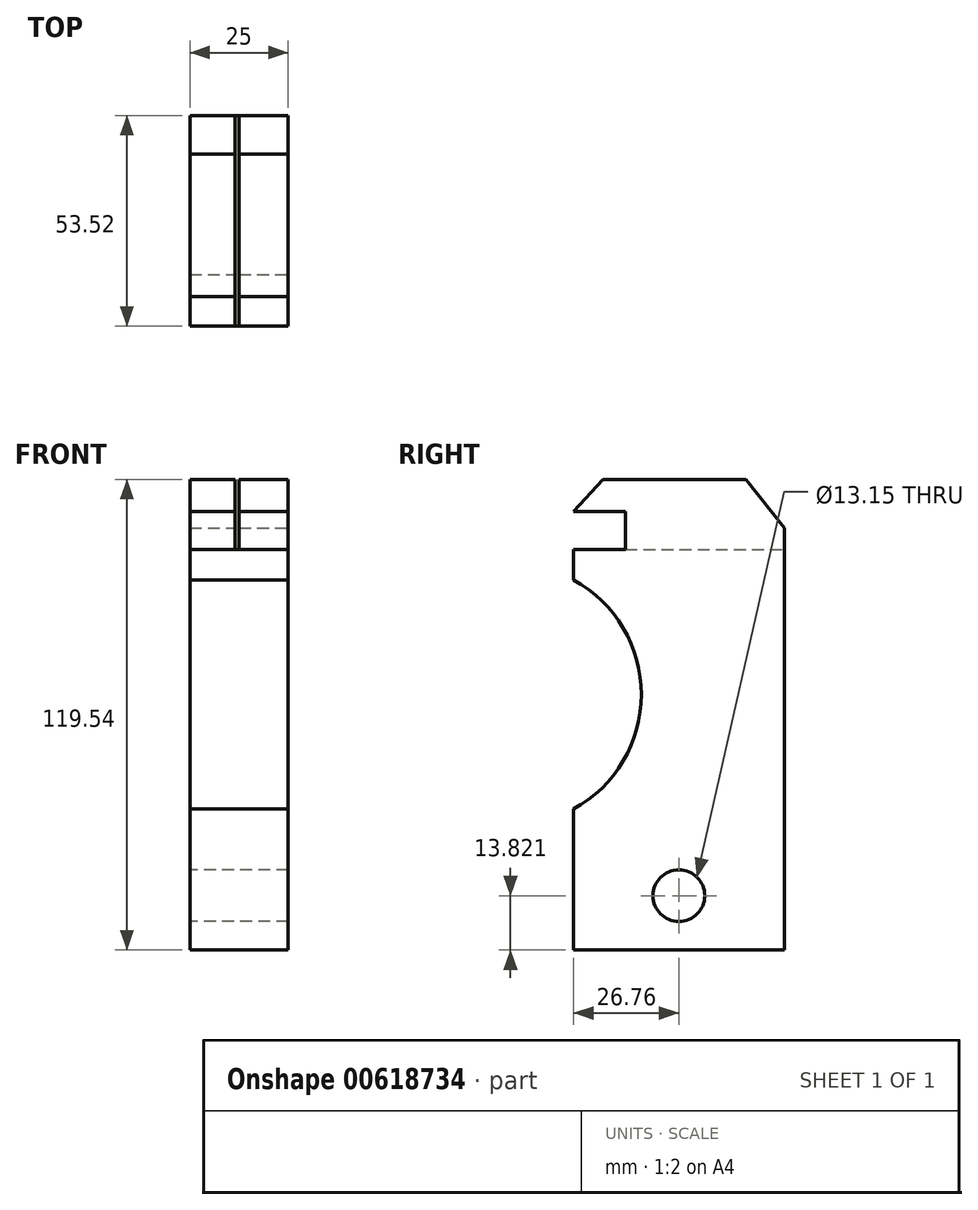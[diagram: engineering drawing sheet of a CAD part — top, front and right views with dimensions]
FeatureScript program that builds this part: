
annotation { "Feature Type Name" : "Feature", "Feature Type Description" : "" }
export const myFeature = defineFeature(function(context is Context, id is Id, definition is map)
    precondition{}
    {
        {
            var Q0;
            Q0=qCreatedBy(makeId("Right.planeOp"),FACE);
            var sketch = newSketch(context, id + "F0", { "sketchPlane" : qUnion([Q0])});
            skLineSegment(sketch, "E0.bottom", {"start": v(-27.84, 57.08) * mm, "end": v(27.84, 57.08) * mm});
            skLineSegment(sketch, "E0.top", {"start": v(-27.84, -57.08) * mm, "end": v(27.84, -57.08) * mm});
            skLineSegment(sketch, "E0.left", {"start": v(-27.84, 57.08) * mm, "end": v(-27.84, -57.08) * mm});
            skLineSegment(sketch, "E0.right", {"start": v(27.84, 57.08) * mm, "end": v(27.84, -57.08) * mm});
            skPoint(sketch, "E0.middle", {"position": v(0, 0) * mm});
            skCircle(sketch, "E1", {"center": v(0, -40.85) * mm, "radius": 5.72 * mm});
            skSolve(sketch);
        }
        {
            var Q0;
            Q0=makeQuery(id+"F0.imprint","IMPRINT",FACE,{"disambiguationData":[TD([[makeQuery(id+"F0.imprint","IMPRINT",EDGE,{"derivedFrom":sQuery(id+"F0.wireOp",EDGE,"E0.bottom")}),-1.0]])]});
            extrude(context, id + "F1", {"entities" : qUnion([Q0]), "depth" : 25 * mm, "offsetDistance" : 25 * mm});
        }
        {
            var Q0;
            Q0=makeQuery(id+"F1.opExtrude","CAP_FACE",FACE,{"disambiguationData":[OSD([sQuery(id+"F0.wireOp",EDGE,"E0.bottom"),sQuery(id+"F0.wireOp",EDGE,"E0.top"),sQuery(id+"F0.wireOp",EDGE,"E0.left"),sQuery(id+"F0.wireOp",EDGE,"E0.right"),sQuery(id+"F0.wireOp",EDGE,"E1")])],"isStart":false});
            var sketch = newSketch(context, id + "F2", { "sketchPlane" : qUnion([Q0])});
            skArc(sketch, "E2", {"start": v(-27.84, -24.75) * mm, "mid": v(-9.54, 3.15) * mm, "end": v(-27.84, 31.06) * mm});
            skSolve(sketch);
        }
        {
            var Q0;
            Q0 = qSketchRegion(id + "F2", true);
            var Q1;
            {var subQ2=sQuery(id+"F2.wireOp",EDGE,"E2");Q1=makeQuery(id+"F2.imprint","IMPRINT",FACE,{"disambiguationData":[TD([[makeQuery(id+"F2.imprint","IMPRINT",EDGE,{"derivedFrom":subQ2}),-1.0]])]});}
            var Q2;
            Q2=makeQuery(id+"F1.opExtrude","CAP_FACE",FACE,{"disambiguationData":[OSD([sQuery(id+"F0.wireOp",EDGE,"E0.bottom"),sQuery(id+"F0.wireOp",EDGE,"E0.top"),sQuery(id+"F0.wireOp",EDGE,"E0.left"),sQuery(id+"F0.wireOp",EDGE,"E0.right"),sQuery(id+"F0.wireOp",EDGE,"E1")])],"isStart":false});
            var Q3;
            Q3=makeQuery(id+"F1.opExtrude","CAP_FACE",FACE,{"disambiguationData":[OSD([sQuery(id+"F0.wireOp",EDGE,"E0.bottom"),sQuery(id+"F0.wireOp",EDGE,"E0.top"),sQuery(id+"F0.wireOp",EDGE,"E0.left"),sQuery(id+"F0.wireOp",EDGE,"E0.right"),sQuery(id+"F0.wireOp",EDGE,"E1")])],"isStart":true});
            extrude(context, id + "F3", {"entities" : qUnion([Q0, Q1, Q2, Q3]), "operationType" : NewBodyOperationType.REMOVE, "oppositeDirection" : true, "depth" : 25 * mm, "offsetDistance" : 25 * mm});
        }
        {
            var Q0;
            Q0=qCreatedBy(makeId("Right.planeOp"),FACE);
            var sketch = newSketch(context, id + "F4", { "sketchPlane" : qUnion([Q0])});
            skLineSegment(sketch, "E3.bottom", {"start": v(-26.76, 59.77) * mm, "end": v(26.76, 59.77) * mm});
            skLineSegment(sketch, "E3.top", {"start": v(-26.76, -59.77) * mm, "end": v(26.76, -59.77) * mm});
            skLineSegment(sketch, "E3.left", {"start": v(-26.76, 59.77) * mm, "end": v(-26.76, -59.77) * mm});
            skLineSegment(sketch, "E3.right", {"start": v(26.76, 59.77) * mm, "end": v(26.76, -59.77) * mm});
            skPoint(sketch, "E3.middle", {"position": v(0, 0) * mm});
            skCircle(sketch, "E4", {"center": v(0, -45.95) * mm, "radius": 6.57 * mm});
            skSolve(sketch);
        }
        {
            var Q0;
            Q0 = qSketchRegion(id + "F4", true);
            extrude(context, id + "F5", {"entities" : qUnion([Q0]), "depth" : 25 * mm, "offsetDistance" : 25 * mm});
        }
        {
            var Q0;
            Q0=makeQuery(id+"F5.opExtrude","CAP_FACE",FACE,{"disambiguationData":[OSD([sQuery(id+"F4.wireOp",EDGE,"E3.bottom"),sQuery(id+"F4.wireOp",EDGE,"E3.top"),sQuery(id+"F4.wireOp",EDGE,"E3.left"),sQuery(id+"F4.wireOp",EDGE,"E3.right"),sQuery(id+"F4.wireOp",EDGE,"E4")])],"isStart":false});
            var sketch = newSketch(context, id + "F6", { "sketchPlane" : qUnion([Q0])});
            skArc(sketch, "E5", {"start": v(-26.76, -23.95) * mm, "mid": v(-9.55, 5.17) * mm, "end": v(-26.76, 34.28) * mm});
            skSolve(sketch);
        }
        {
            var Q0;
            Q0 = qSketchRegion(id + "F6", true);
            var Q1;
            {var subQ0=sQuery(id+"F6.wireOp",EDGE,"E5");Q1=makeQuery(id+"F6.imprint","IMPRINT",FACE,{"disambiguationData":[TD([[makeQuery(id+"F6.imprint","IMPRINT",EDGE,{"derivedFrom":subQ0}),1.0]])]});}
            extrude(context, id + "F7", {"entities" : qUnion([Q0, Q1]), "operationType" : NewBodyOperationType.REMOVE, "oppositeDirection" : true, "depth" : 25 * mm, "offsetDistance" : 25 * mm});
        }
        {
            var Q0;
            Q0=makeQuery(id+"F5.opExtrude","CAP_FACE",FACE,{"disambiguationData":[OSD([sQuery(id+"F4.wireOp",EDGE,"E3.bottom"),sQuery(id+"F4.wireOp",EDGE,"E3.top"),sQuery(id+"F4.wireOp",EDGE,"E3.left"),sQuery(id+"F4.wireOp",EDGE,"E3.right"),sQuery(id+"F4.wireOp",EDGE,"E4")])],"isStart":false});
            var sketch = newSketch(context, id + "F8", { "sketchPlane" : qUnion([Q0])});
            skLineSegment(sketch, "E6", {"start": v(-26.76, 42.06) * mm, "end": v(-13.62, 42.06) * mm});
            skLineSegment(sketch, "E7", {"start": v(-13.62, 42.06) * mm, "end": v(-13.62, 51.72) * mm});
            skLineSegment(sketch, "E8", {"start": v(-13.62, 51.72) * mm, "end": v(-26.76, 51.72) * mm});
            skSolve(sketch);
        }
        {
            var Q0;
            Q0 = qSketchRegion(id + "F8", true);
            var Q1;
            {var subQ0=sQuery(id+"F8.wireOp",EDGE,"E6");Q1=makeQuery(id+"F8.imprint","IMPRINT",FACE,{"disambiguationData":[TD([[makeQuery(id+"F8.imprint","IMPRINT",EDGE,{"derivedFrom":subQ0}),1.0]])]});}
            extrude(context, id + "F9", {"entities" : qUnion([Q0, Q1]), "operationType" : NewBodyOperationType.REMOVE, "oppositeDirection" : true, "depth" : 25 * mm, "offsetDistance" : 25 * mm});
        }
        {
            var Q0;
            Q0=makeQuery(id+"F5.opExtrude","CAP_FACE",FACE,{"disambiguationData":[OSD([sQuery(id+"F4.wireOp",EDGE,"E3.bottom"),sQuery(id+"F4.wireOp",EDGE,"E3.top"),sQuery(id+"F4.wireOp",EDGE,"E3.left"),sQuery(id+"F4.wireOp",EDGE,"E3.right"),sQuery(id+"F4.wireOp",EDGE,"E4")])],"isStart":false});
            var sketch = newSketch(context, id + "F10", { "sketchPlane" : qUnion([Q0])});
            skLineSegment(sketch, "E9", {"start": v(-26.76, -47.3) * mm, "end": v(-16.57, -59.77) * mm});
            skLineSegment(sketch, "E10", {"start": v(15.36, -59.77) * mm, "end": v(26.76, -50.78) * mm});
            skLineSegment(sketch, "E11", {"start": v(26.76, 49.57) * mm, "end": v(18.58, 59.77) * mm});
            skLineSegment(sketch, "E12", {"start": v(-26.76, 51.72) * mm, "end": v(-19.25, 59.77) * mm});
            skSolve(sketch);
        }
        {
            var Q0;
            Q0 = qSketchRegion(id + "F10", true);
            var Q1;
            {var subQ0=sQuery(id+"F10.wireOp",EDGE,"E12");Q1=makeQuery(id+"F10.imprint","IMPRINT",FACE,{"disambiguationData":[TD([[makeQuery(id+"F10.imprint","IMPRINT",EDGE,{"derivedFrom":subQ0}),1.0]])]});}
            extrude(context, id + "F11", {"entities" : qUnion([Q0, Q1]), "operationType" : NewBodyOperationType.REMOVE, "oppositeDirection" : true, "depth" : 25 * mm, "offsetDistance" : 25 * mm});
        }
        {
            var Q0;
            Q0=makeQuery(id+"F5.opExtrude","CAP_FACE",FACE,{"disambiguationData":[OSD([sQuery(id+"F4.wireOp",EDGE,"E3.bottom"),sQuery(id+"F4.wireOp",EDGE,"E3.top"),sQuery(id+"F4.wireOp",EDGE,"E3.left"),sQuery(id+"F4.wireOp",EDGE,"E3.right"),sQuery(id+"F4.wireOp",EDGE,"E4")])],"isStart":false});
            var sketch = newSketch(context, id + "F12", { "sketchPlane" : qUnion([Q0])});
            skLineSegment(sketch, "E13", {"start": v(16.97, 59.77) * mm, "end": v(26.76, 47.42) * mm});
            skSolve(sketch);
        }
        {
            var Q0;
            Q0 = qSketchRegion(id + "F12", true);
            var Q1;
            {var subQ0=sQuery(id+"F12.wireOp",EDGE,"E13");Q1=makeQuery(id+"F12.imprint","IMPRINT",FACE,{"disambiguationData":[TD([[makeQuery(id+"F12.imprint","IMPRINT",EDGE,{"derivedFrom":subQ0}),1.0]])]});}
            extrude(context, id + "F13", {"entities" : qUnion([Q0, Q1]), "operationType" : NewBodyOperationType.REMOVE, "oppositeDirection" : true, "depth" : 25 * mm, "offsetDistance" : 25 * mm});
        }
        {
            var Q0;
            Q0=makeQuery(id+"F5.opExtrude","SWEPT_FACE",FACE,{"disambiguationData":[OSD([sQuery(id+"F4.wireOp",EDGE,"E3.bottom")])]});
            var sketch = newSketch(context, id + "F14", { "sketchPlane" : qUnion([Q0])});
            skLineSegment(sketch, "E14", {"start": v(12.5, 16.97) * mm, "end": v(12.5, -19.25) * mm});
            skLineSegment(sketch, "E15", {"start": v(11.5, -19.25) * mm, "end": v(11.5, 16.97) * mm});
            skLineSegment(sketch, "E16", {"start": v(11.5, -19.25) * mm, "end": v(11.5, -42.41) * mm});
            skLineSegment(sketch, "E17", {"start": v(11.5, -42.41) * mm, "end": v(12.5, -42.41) * mm});
            skLineSegment(sketch, "E18", {"start": v(12.5, -42.41) * mm, "end": v(12.5, -19.25) * mm});
            skLineSegment(sketch, "E19", {"start": v(12.5, 16.97) * mm, "end": v(12.5, 39.22) * mm});
            skLineSegment(sketch, "E20", {"start": v(12.5, 39.22) * mm, "end": v(11.5, 39.22) * mm});
            skLineSegment(sketch, "E21", {"start": v(11.5, 39.22) * mm, "end": v(11.5, 16.97) * mm});
            skSolve(sketch);
        }
        {
            var Q0;
            Q0 = qSketchRegion(id + "F14", true);
            var Q1;
            Q1=makeQuery(id+"F9.boolean.opBoolean","COPY",FACE,{"derivedFrom":makeQuery(id+"F9.opExtrude","SWEPT_FACE",FACE,{"disambiguationData":[OSD([sQuery(id+"F8.wireOp",EDGE,"E6")])]})});
            extrude(context, id + "F15", {"entities" : qUnion([Q0]), "operationType" : NewBodyOperationType.REMOVE, "endBound" : BoundingType.UP_TO_SURFACE, "oppositeDirection" : true, "depth" : 15.3 * mm, "endBoundEntityFace" : qUnion([Q1]), "offsetDistance" : 25 * mm});
        }
    });
